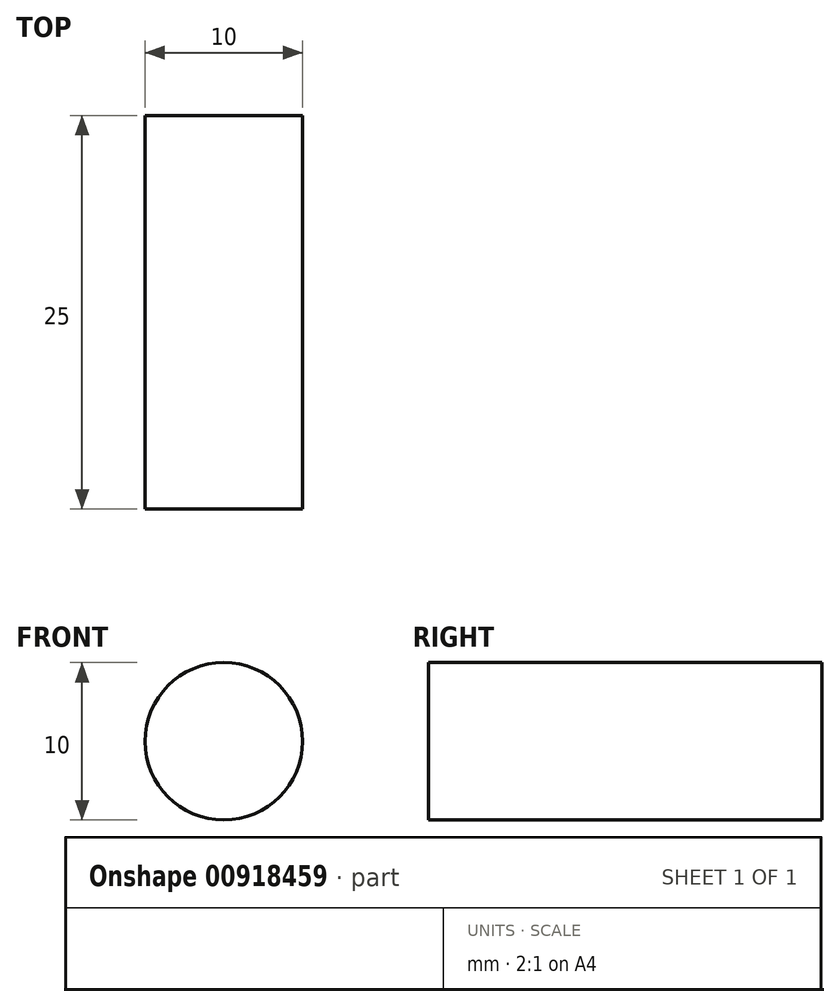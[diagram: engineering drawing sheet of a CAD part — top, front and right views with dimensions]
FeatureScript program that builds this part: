
annotation { "Feature Type Name" : "Feature", "Feature Type Description" : "" }
export const myFeature = defineFeature(function(context is Context, id is Id, definition is map)
    precondition{}
    {
        {
            var Q0;
            Q0=qCreatedBy(makeId("Front.planeOp"),FACE);
            var sketch = newSketch(context, id + "F0", { "sketchPlane" : qUnion([Q0])});
            skCircle(sketch, "E0", {"center": v(0, 0) * mm, "radius": 5 * mm});
            skSolve(sketch);
        }
        {
            var Q0;
            Q0=makeQuery(id+"F0.imprint","IMPRINT",FACE,{"disambiguationData":[TD([[makeQuery(id+"F0.imprint","IMPRINT",EDGE,{"derivedFrom":sQuery(id+"F0.wireOp",EDGE,"E0")}),1.0]])]});
            extrude(context, id + "F1", {"entities" : qUnion([Q0]), "endBound" : BoundingType.SYMMETRIC, "depth" : 25 * mm, "offsetDistance" : 25 * mm});
        }
    });
